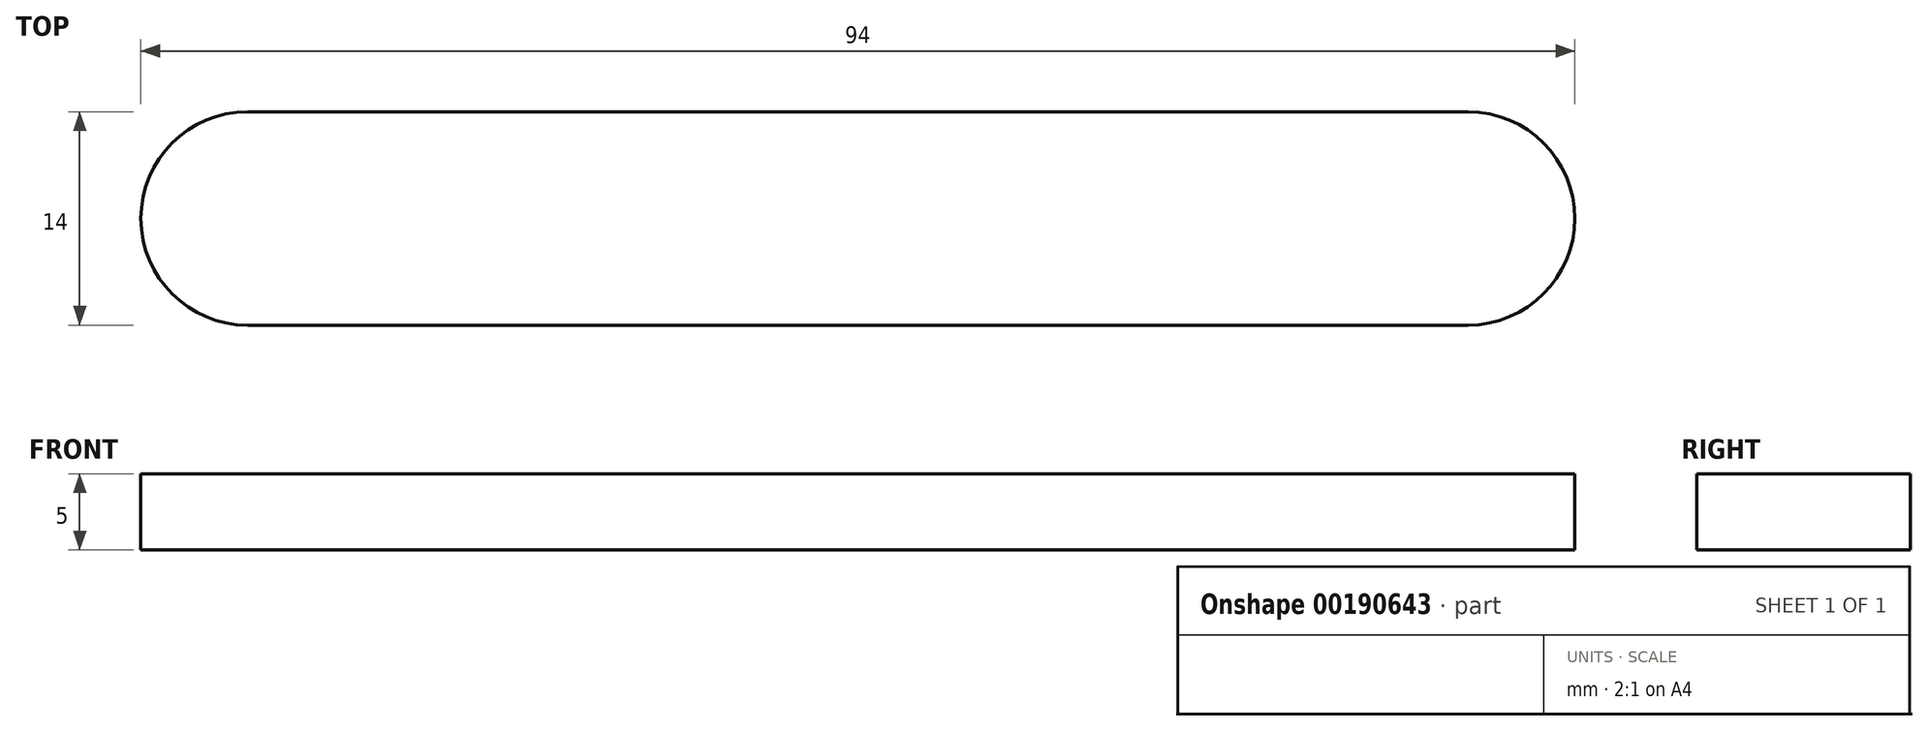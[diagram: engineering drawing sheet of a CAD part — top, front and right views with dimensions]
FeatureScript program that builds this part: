
annotation { "Feature Type Name" : "Feature", "Feature Type Description" : "" }
export const myFeature = defineFeature(function(context is Context, id is Id, definition is map)
    precondition{}
    {
        {
            var Q0;
            Q0=qCreatedBy(makeId("Top.planeOp"),FACE);
            var sketch = newSketch(context, id + "F0", { "sketchPlane" : qUnion([Q0])});
            skLineSegment(sketch, "E0", {"start": v(0, 7) * mm, "end": v(80, 7) * mm});
            skArc(sketch, "E1", {"start": v(80, -7) * mm, "mid": v(87, 0) * mm, "end": v(80, 7) * mm});
            skLineSegment(sketch, "E2", {"start": v(80, -7) * mm, "end": v(0, -7) * mm});
            skArc(sketch, "E3", {"start": v(0, 7) * mm, "mid": v(-7, 0) * mm, "end": v(0, -7) * mm});
            skSolve(sketch);
        }
        {
            var Q0;
            Q0=makeQuery(id+"F0.imprint","IMPRINT",FACE,{"disambiguationData":[TD([[makeQuery(id+"F0.imprint","IMPRINT",EDGE,{"derivedFrom":sQuery(id+"F0.wireOp",EDGE,"E0")}),-1.0]])]});
            extrude(context, id + "F1", {"entities" : qUnion([Q0]), "depth" : 5 * mm});
        }
    });
